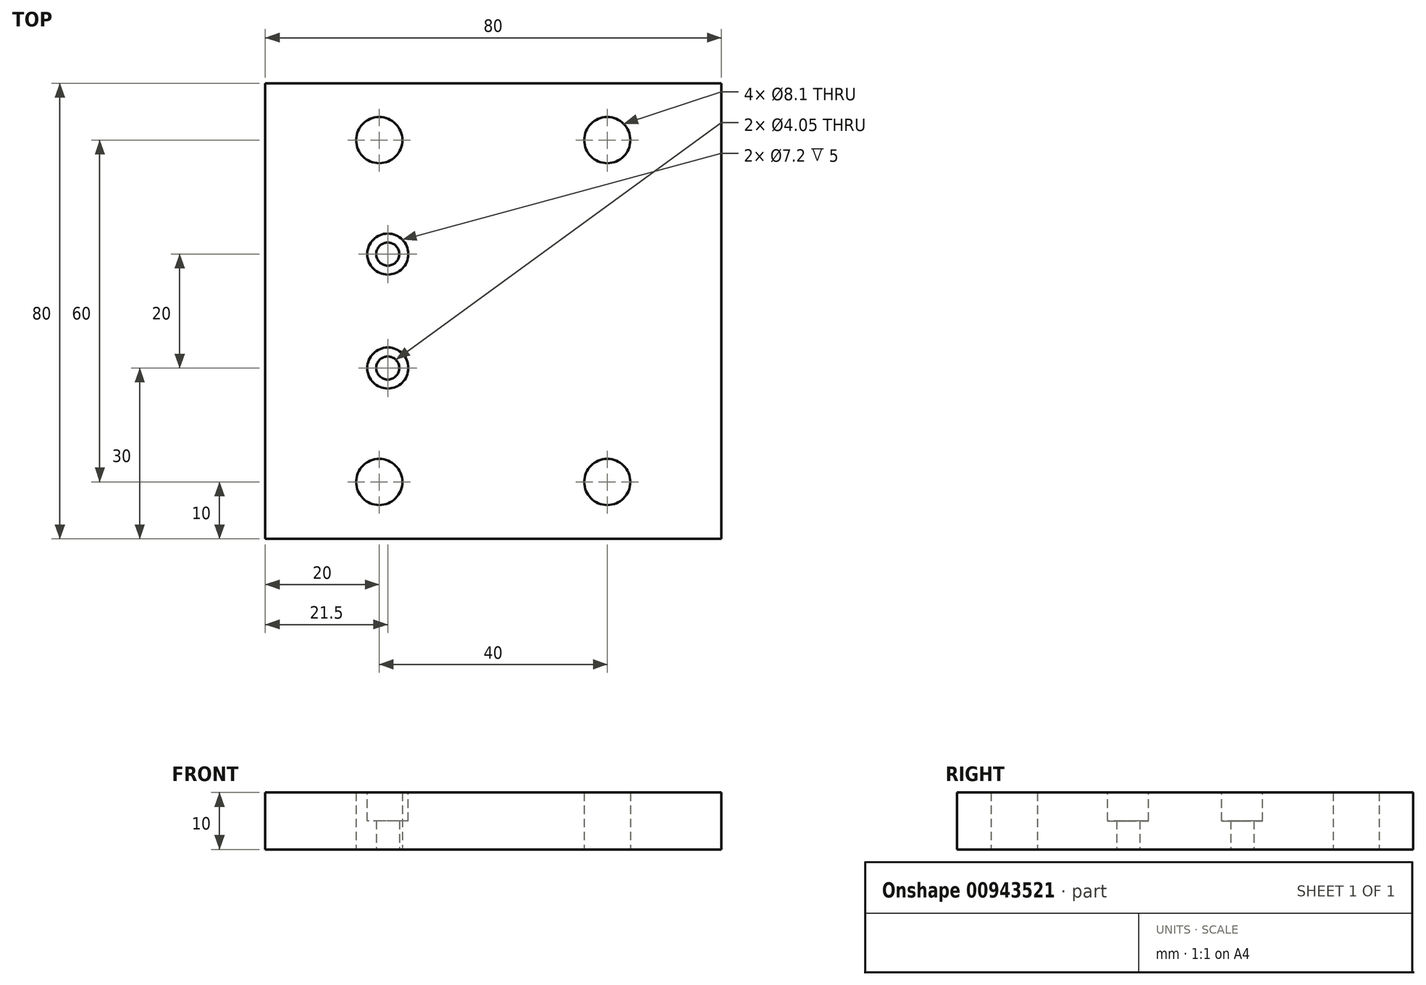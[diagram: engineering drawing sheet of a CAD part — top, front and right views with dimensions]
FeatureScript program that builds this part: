
annotation { "Feature Type Name" : "Feature", "Feature Type Description" : "" }
export const myFeature = defineFeature(function(context is Context, id is Id, definition is map)
    precondition{}
    {
        {
            var Q0;
            Q0=qCreatedBy(makeId("Top.planeOp"),FACE);
            var sketch = newSketch(context, id + "F0", { "sketchPlane" : qUnion([Q0])});
            skLineSegment(sketch, "E0.bottom", {"start": v(0, 0) * mm, "end": v(80, 0) * mm});
            skLineSegment(sketch, "E0.top", {"start": v(0, -80) * mm, "end": v(80, -80) * mm});
            skLineSegment(sketch, "E0.left", {"start": v(0, 0) * mm, "end": v(0, -80) * mm});
            skLineSegment(sketch, "E0.right", {"start": v(80, 0) * mm, "end": v(80, -80) * mm});
            skLineSegment(sketch, "E1", {"start": v(0, -80) * mm, "end": v(58.5, -80) * mm, "construction": true});
            skLineSegment(sketch, "E2", {"start": v(0, -80) * mm, "end": v(0, -70) * mm, "construction": true});
            skLineSegment(sketch, "E3", {"start": v(0, -70) * mm, "end": v(0, -10) * mm, "construction": true});
            skLineSegment(sketch, "E4", {"start": v(0, -70) * mm, "end": v(20, -70) * mm, "construction": true});
            skLineSegment(sketch, "E5", {"start": v(20, -70) * mm, "end": v(60, -70) * mm, "construction": true});
            skLineSegment(sketch, "E6", {"start": v(0, -10) * mm, "end": v(20, -10) * mm, "construction": true});
            skLineSegment(sketch, "E7", {"start": v(20, -10) * mm, "end": v(60, -10) * mm, "construction": true});
            skCircle(sketch, "E8", {"center": v(20, -70) * mm, "radius": 4.05 * mm});
            skCircle(sketch, "E9", {"center": v(60, -70) * mm, "radius": 4.05 * mm});
            skCircle(sketch, "E10", {"center": v(20, -10) * mm, "radius": 4.05 * mm});
            skCircle(sketch, "E11", {"center": v(60, -10) * mm, "radius": 4.05 * mm});
            skLineSegment(sketch, "E12", {"start": v(0, 0) * mm, "end": v(0, -40) * mm, "construction": true});
            skLineSegment(sketch, "E13", {"start": v(0, -40) * mm, "end": v(21.5, -40) * mm, "construction": true});
            skLineSegment(sketch, "E14", {"start": v(21.5, -40) * mm, "end": v(21.5, -50) * mm, "construction": true});
            skLineSegment(sketch, "E15", {"start": v(21.5, -50) * mm, "end": v(21.5, -30) * mm, "construction": true});
            skPoint(sketch, "E15.endSnap0", {"position": v(21.5, -45) * mm});
            skCircle(sketch, "E16", {"center": v(21.5, -50) * mm, "radius": 2.02 * mm});
            skCircle(sketch, "E17", {"center": v(21.5, -30) * mm, "radius": 2.02 * mm});
            skSolve(sketch);
        }
        {
            var Q0;
            Q0 = qSketchRegion(id + "F0", true);
            extrude(context, id + "F1", {"entities" : qUnion([Q0]), "depth" : 10 * mm, "offsetDistance" : 25 * mm});
        }
        {
            var Q0;
            Q0=makeQuery(id+"F1.opExtrude","CAP_FACE",FACE,{"disambiguationData":[OSD([sQuery(id+"F0.wireOp",EDGE,"E0.bottom"),sQuery(id+"F0.wireOp",EDGE,"E0.top"),sQuery(id+"F0.wireOp",EDGE,"E0.left"),sQuery(id+"F0.wireOp",EDGE,"E0.right"),sQuery(id+"F0.wireOp",EDGE,"E8"),sQuery(id+"F0.wireOp",EDGE,"E9"),sQuery(id+"F0.wireOp",EDGE,"E10"),sQuery(id+"F0.wireOp",EDGE,"E11"),sQuery(id+"F0.wireOp",EDGE,"E16"),sQuery(id+"F0.wireOp",EDGE,"E17")])],"isStart":false});
            var sketch = newSketch(context, id + "F2", { "sketchPlane" : qUnion([Q0])});
            skCircle(sketch, "E18", {"center": v(21.5, -30) * mm, "radius": 3.6 * mm});
            skCircle(sketch, "E19", {"center": v(21.5, -50) * mm, "radius": 3.6 * mm});
            skSolve(sketch);
        }
        {
            var Q0;
            Q0 = qSketchRegion(id + "F2", true);
            extrude(context, id + "F3", {"entities" : qUnion([Q0]), "operationType" : NewBodyOperationType.REMOVE, "oppositeDirection" : true, "depth" : 5 * mm, "offsetDistance" : 25 * mm});
        }
    });
